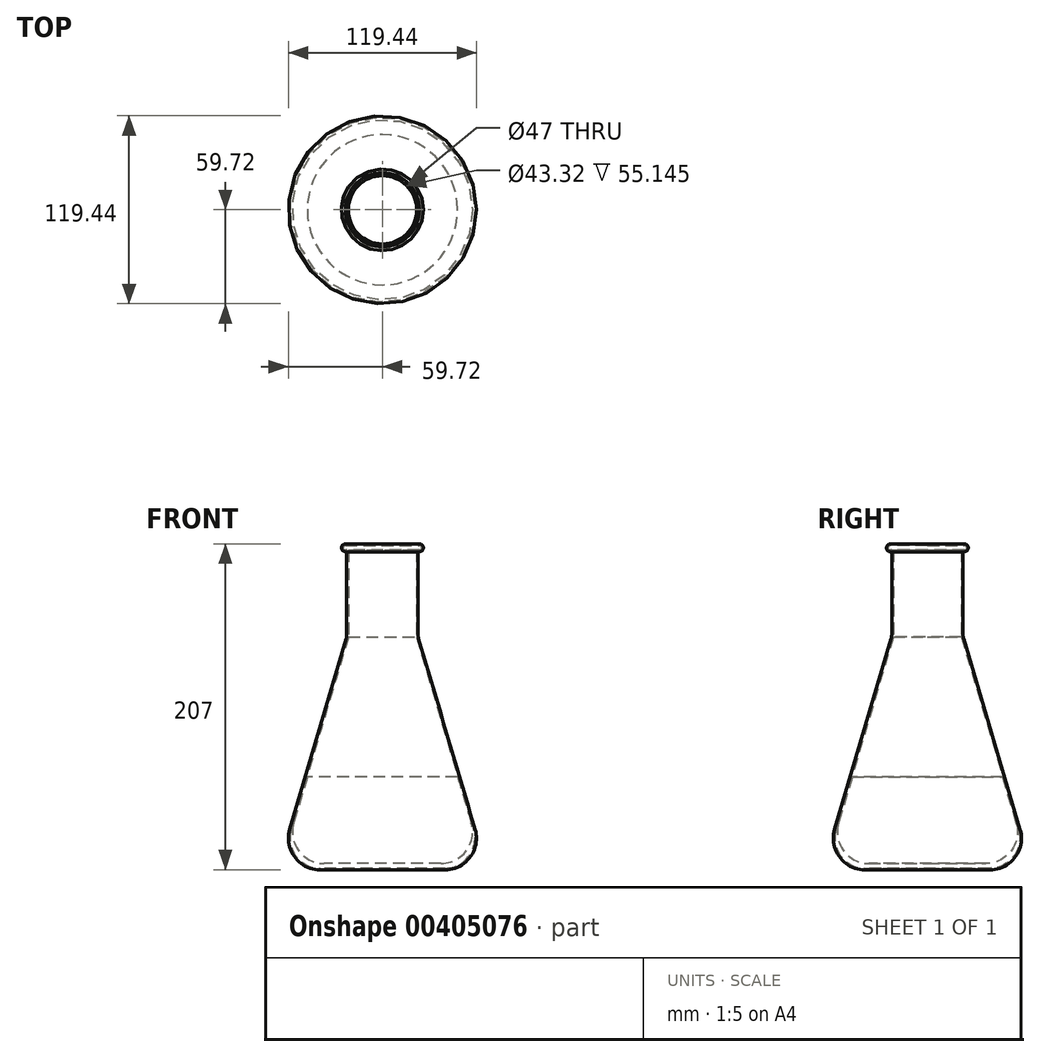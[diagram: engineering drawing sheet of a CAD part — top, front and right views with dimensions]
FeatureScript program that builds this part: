
annotation { "Feature Type Name" : "Feature", "Feature Type Description" : "" }
export const myFeature = defineFeature(function(context is Context, id is Id, definition is map)
    precondition{}
    {
        {
            var Q0;
            Q0=qCreatedBy(makeId("Top.planeOp"),FACE);
            cPlane(context, id + "F0", {"entities" : qUnion([Q0]), "cplaneType" : CPlaneType.OFFSET, "offset" : 4 * mm, "width" : 150 * mm, "height" : 150 * mm});
        }
        {
            var Q0;
            Q0=qCreatedBy(id+"F0.planeOp",FACE);
            var sketch = newSketch(context, id + "F1", { "sketchPlane" : qUnion([Q0])});
            skCircle(sketch, "E0", {"center": v(0, 0) * mm, "radius": 66.25 * mm});
            skCircle(sketch, "E1", {"center": v(0, 0) * mm, "radius": 64 * mm});
            skSolve(sketch);
        }
        {
            var Q0;
            Q0=makeQuery(id+"F1.imprint","IMPRINT",FACE,{"disambiguationData":[TD([[makeQuery(id+"F1.imprint","IMPRINT",EDGE,{"derivedFrom":sQuery(id+"F1.wireOp",EDGE,"E1")}),1.0]])]});
            extrude(context, id + "F2", {"entities" : qUnion([Q0]), "depth" : 55 * mm, "hasDraft" : true, "draftAngle" : 16.5 * degree, "draftPullDirection" : true});
        }
        {
            var Q0;
            Q0=qCreatedBy(makeId("Top.planeOp"),FACE);
            var sketch = newSketch(context, id + "F3", { "sketchPlane" : qUnion([Q0])});
            skCircle(sketch, "E2", {"center": v(0, 0) * mm, "radius": 66.5 * mm});
            skSolve(sketch);
        }
        {
            var Q0;
            Q0 = qSketchRegion(id + "F3", true);
            extrude(context, id + "F4", {"entities" : qUnion([Q0]), "depth" : 148 * mm, "hasDraft" : true, "draftAngle" : 16.5 * degree, "draftPullDirection" : true});
        }
        {
            var Q0;
            Q0=makeQuery(id+"F4.opExtrude","CAP_FACE",FACE,{"disambiguationData":[OSD([sQuery(id+"F3.wireOp",EDGE,"E2")])],"isStart":true});
            fillet(context, id + "F5", {"entities" : qUnion([Q0]), "radius" : 20 * mm, "tangentPropagation" : true, "allowEdgeOverflow" : false});
        }
        {
            var Q0;
            Q0=makeQuery(id+"F2.opExtrude","CAP_EDGE",EDGE,{"disambiguationData":[OSD([sQuery(id+"F1.wireOp",EDGE,"E1")])],"isStart":true});
            fillet(context, id + "F6", {"entities" : qUnion([Q0]), "radius" : 20 * mm, "tangentPropagation" : true, "allowEdgeOverflow" : false});
        }
        {
            var Q0;
            Q0=makeQuery(id+"F4.opExtrude","CAP_FACE",FACE,{"disambiguationData":[OSD([sQuery(id+"F3.wireOp",EDGE,"E2")])],"isStart":false});
            var sketch = newSketch(context, id + "F7", { "sketchPlane" : qUnion([Q0])});
            skCircle(sketch, "E3.0", {"center": v(0, 0) * mm, "radius": 22.66 * mm});
            skSolve(sketch);
        }
        {
            var Q0;
            Q0=makeQuery(id+"F7.imprint","IMPRINT",FACE,{"disambiguationData":[TD([[makeQuery(id+"F7.imprint","IMPRINT",EDGE,{"derivedFrom":sQuery(id+"F7.wireOp",EDGE,"E3.0")}),1.0]])]});
            extrude(context, id + "F8", {"entities" : qUnion([Q0]), "operationType" : NewBodyOperationType.ADD, "depth" : 54 * mm});
        }
        {
            var Q0;
            Q0=makeQuery(id+"F8.opExtrude","CAP_FACE",FACE,{"disambiguationData":[OSD([sQuery(id+"F7.wireOp",EDGE,"E3.0")])],"isStart":false});
            var sketch = newSketch(context, id + "F9", { "sketchPlane" : qUnion([Q0])});
            skCircle(sketch, "E4", {"center": v(0, 0) * mm, "radius": 26 * mm});
            skSolve(sketch);
        }
        {
            var Q0;
            Q0 = qSketchRegion(id + "F9", true);
            extrude(context, id + "F10", {"entities" : qUnion([Q0]), "operationType" : NewBodyOperationType.ADD, "depth" : 5 * mm});
        }
        {
            var Q0;
            Q0=makeQuery(id+"F10.opExtrude","CAP_EDGE",EDGE,{"disambiguationData":[OSD([sQuery(id+"F9.wireOp",EDGE,"E4")])],"isStart":false});
            var Q1;
            Q1=makeQuery(id+"F10.opExtrude","CAP_EDGE",EDGE,{"disambiguationData":[OSD([sQuery(id+"F9.wireOp",EDGE,"E4")])],"isStart":true});
            fillet(context, id + "F11", {"entities" : qUnion([Q0, Q1]), "radius" : 2.5 * mm, "tangentPropagation" : true, "allowEdgeOverflow" : false});
        }
        {
            var Q0;
            Q0=makeQuery(id+"F10.opExtrude","CAP_FACE",FACE,{"disambiguationData":[OSD([sQuery(id+"F9.wireOp",EDGE,"E4")])],"isStart":false});
            shell(context, id + "F12", {"entities" : qUnion([Q0]), "thickness" : 1 * mm});
        }
        {
            var Q0;
            Q0=makeQuery(id+"F8.boolean.opBoolean","MERGE",EDGE,{"derivedFrom":[makeQuery(id+"F4.opExtrude","CAP_EDGE",EDGE,{"disambiguationData":[OSD([sQuery(id+"F3.wireOp",EDGE,"E2")])],"isStart":false}),makeQuery(id+"F8.opExtrude","CAP_EDGE",EDGE,{"disambiguationData":[OSD([sQuery(id+"F7.wireOp",EDGE,"E3.0")])],"isStart":true})]});
            fillet(context, id + "F13", {"entities" : qUnion([Q0]), "radius" : 10 * mm, "tangentPropagation" : true, "allowEdgeOverflow" : false});
        }
    });
